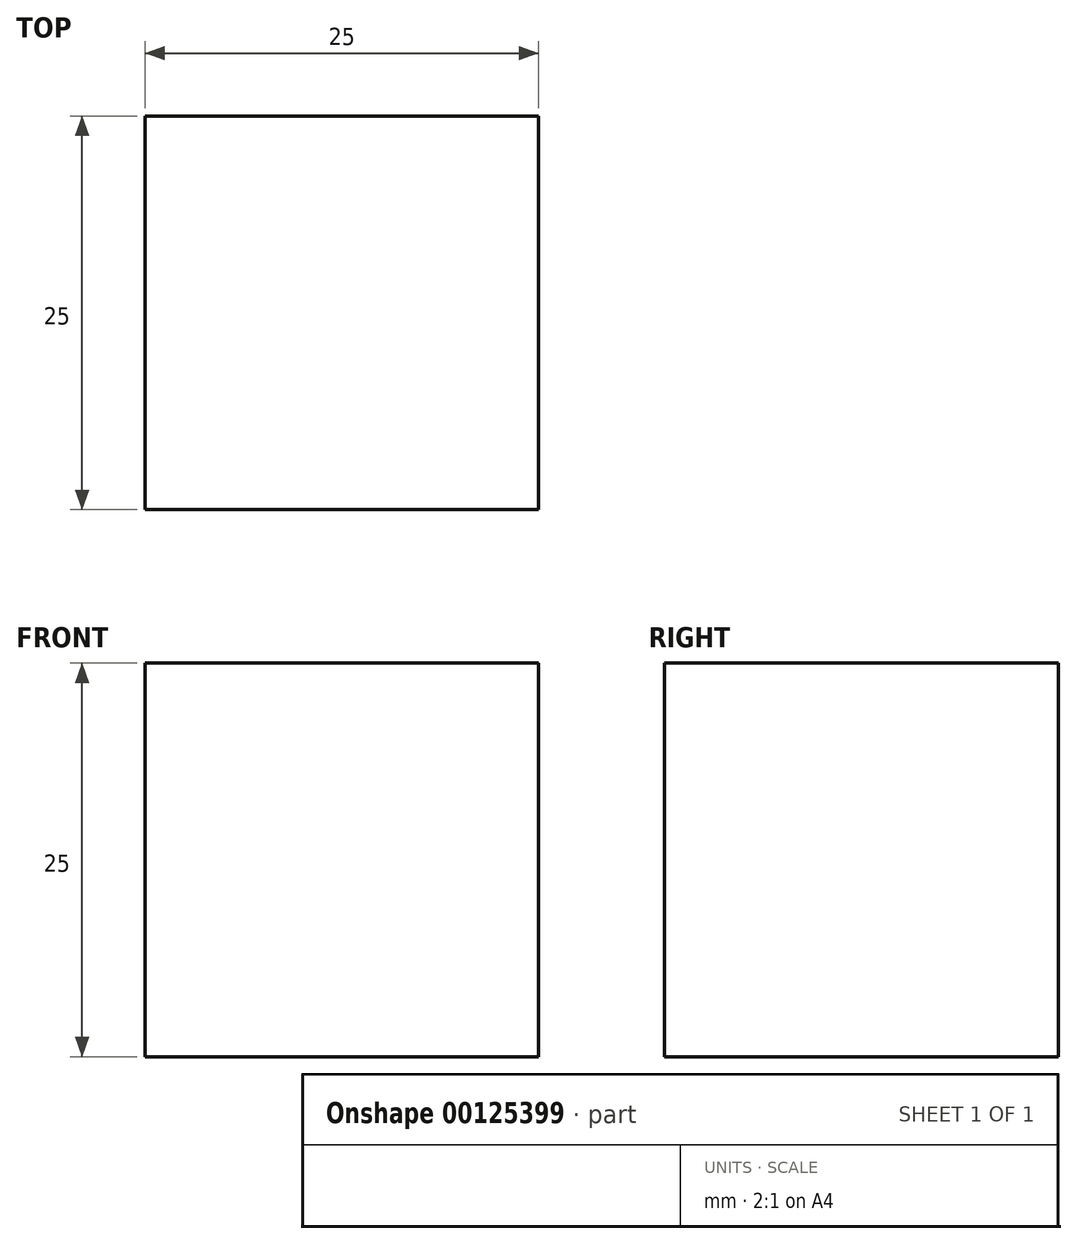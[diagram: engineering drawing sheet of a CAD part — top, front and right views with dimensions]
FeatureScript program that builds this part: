
annotation { "Feature Type Name" : "Feature", "Feature Type Description" : "" }
export const myFeature = defineFeature(function(context is Context, id is Id, definition is map)
    precondition{}
    {
        {
            var Q0;
            Q0=qCreatedBy(makeId("Top.planeOp"),FACE);
            var sketch = newSketch(context, id + "F0", { "sketchPlane" : qUnion([Q0])});
            skLineSegment(sketch, "E0.bottom", {"start": v(12.5, -12.5) * mm, "end": v(-12.5, -12.5) * mm});
            skLineSegment(sketch, "E0.top", {"start": v(12.5, 12.5) * mm, "end": v(-12.5, 12.5) * mm});
            skLineSegment(sketch, "E0.left", {"start": v(12.5, -12.5) * mm, "end": v(12.5, 12.5) * mm});
            skLineSegment(sketch, "E0.right", {"start": v(-12.5, -12.5) * mm, "end": v(-12.5, 12.5) * mm});
            skPoint(sketch, "E0.middle", {"position": v(0, 0) * mm});
            skSolve(sketch);
        }
        {
            var Q0;
            Q0 = qSketchRegion(id + "F0", true);
            extrude(context, id + "F1", {"entities" : qUnion([Q0]), "depth" : 25 * mm});
        }
    });
